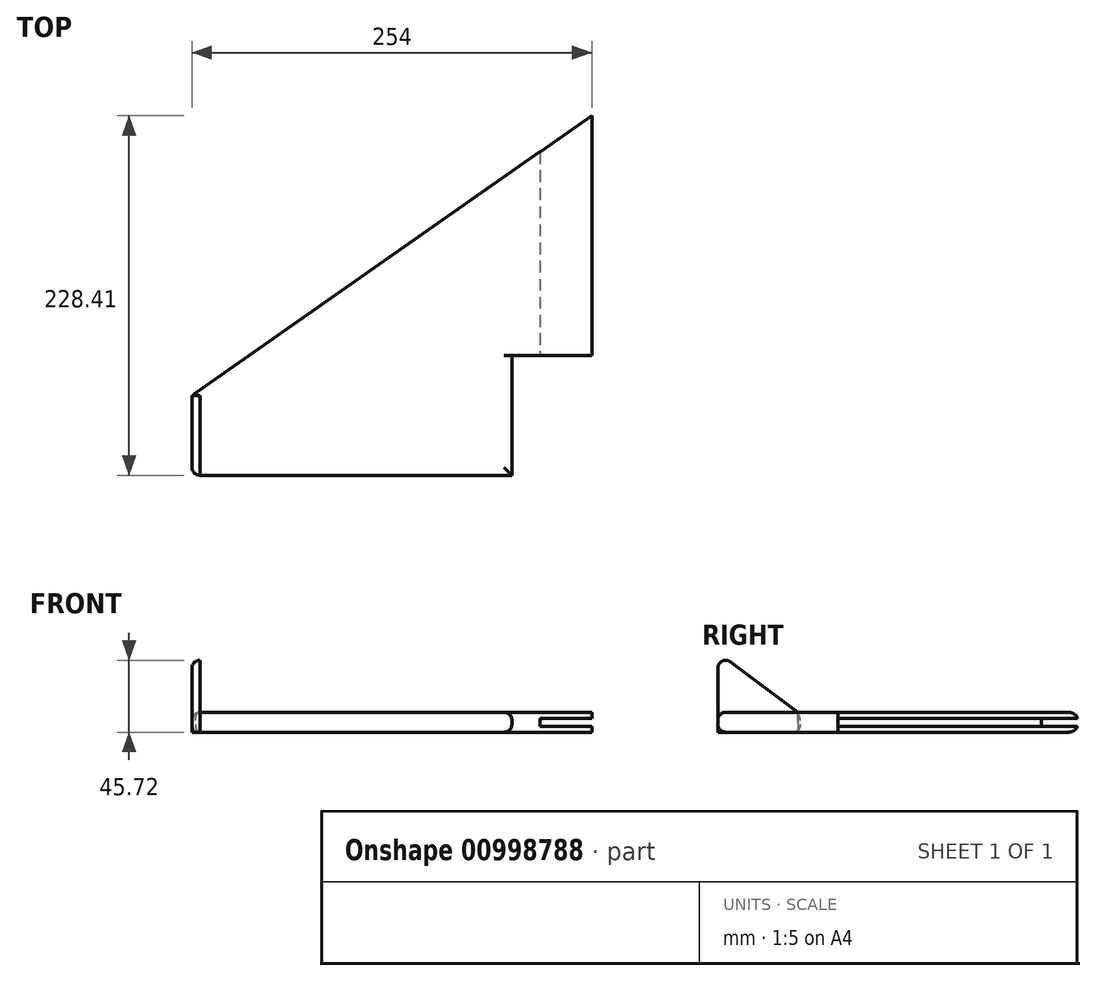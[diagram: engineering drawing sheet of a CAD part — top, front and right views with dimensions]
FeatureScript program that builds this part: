
annotation { "Feature Type Name" : "Feature", "Feature Type Description" : "" }
export const myFeature = defineFeature(function(context is Context, id is Id, definition is map)
    precondition{}
    {
        {
            var Q0;
            Q0=qCreatedBy(makeId("Top.planeOp"),FACE);
            var sketch = newSketch(context, id + "F0", { "sketchPlane" : qUnion([Q0])});
            skLineSegment(sketch, "E0", {"start": v(85.13, 123.88) * mm, "end": v(85.13, -28.52) * mm});
            skLineSegment(sketch, "E1", {"start": v(85.13, -28.52) * mm, "end": v(34.33, -28.52) * mm});
            skLineSegment(sketch, "E2", {"start": v(34.33, -28.52) * mm, "end": v(34.33, -104.72) * mm});
            skLineSegment(sketch, "E3", {"start": v(34.33, -104.72) * mm, "end": v(-168.87, -104.72) * mm});
            skLineSegment(sketch, "E4", {"start": v(-168.87, -104.72) * mm, "end": v(-168.87, -53.92) * mm});
            skLineSegment(sketch, "E5", {"start": v(-168.87, -53.92) * mm, "end": v(85.13, 123.88) * mm});
            skSolve(sketch);
        }
        {
            var Q0;
            Q0=makeQuery(id+"F0.imprint","IMPRINT",FACE,{"disambiguationData":[TD([[makeQuery(id+"F0.imprint","IMPRINT",EDGE,{"derivedFrom":sQuery(id+"F0.wireOp",EDGE,"E0")}),-1.0]])]});
            extrude(context, id + "F1", {"entities" : qUnion([Q0]), "depth" : 12.7 * mm, "offsetDistance" : 25.4 * mm});
        }
        {
            var Q0;
            Q0=makeQuery(id+"F1.opExtrude","SWEPT_FACE",FACE,{"disambiguationData":[OSD([sQuery(id+"F0.wireOp",EDGE,"E4")])]});
            var sketch = newSketch(context, id + "F2", { "sketchPlane" : qUnion([Q0])});
            skLineSegment(sketch, "E6", {"start": v(53.92, 0) * mm, "end": v(53.92, 12.7) * mm});
            skLineSegment(sketch, "E7", {"start": v(53.92, 12.7) * mm, "end": v(104.72, 12.7) * mm});
            skLineSegment(sketch, "E8", {"start": v(104.72, 12.7) * mm, "end": v(104.72, 0) * mm});
            skLineSegment(sketch, "E9", {"start": v(104.72, 0) * mm, "end": v(53.92, 0) * mm});
            skLineSegment(sketch, "E10", {"start": v(104.72, 0) * mm, "end": v(104.72, 50.8) * mm});
            skLineSegment(sketch, "E11", {"start": v(104.72, 50.8) * mm, "end": v(53.92, 12.7) * mm});
            skSolve(sketch);
        }
        {
            var Q0;
            Q0=makeQuery(id+"F2.imprint","IMPRINT",FACE,{"disambiguationData":[TD([[makeQuery(id+"F2.imprint","IMPRINT",EDGE,{"derivedFrom":sQuery(id+"F2.wireOp",EDGE,"E7")}),-1.0]])]});
            var Q1;
            Q1=makeQuery(id+"F2.imprint","IMPRINT",FACE,{"disambiguationData":[TD([[makeQuery(id+"F2.imprint","IMPRINT",EDGE,{"derivedFrom":sQuery(id+"F2.wireOp",EDGE,"E6")}),1.0]])]});
            extrude(context, id + "F3", {"entities" : qUnion([Q0, Q1]), "oppositeDirection" : true, "depth" : 5.08 * mm, "offsetDistance" : 25.4 * mm});
        }
        {
            var Q0;
            Q0=makeQuery(id+"F1.opExtrude","CAP_EDGE",EDGE,{"disambiguationData":[OSD([sQuery(id+"F0.wireOp",EDGE,"E5")])],"isStart":false});
            var Q1;
            Q1=makeQuery(id+"F1.opExtrude","CAP_EDGE",EDGE,{"disambiguationData":[OSD([sQuery(id+"F0.wireOp",EDGE,"E5")])],"isStart":true});
            var Q2;
            Q2=makeQuery(id+"F1.opExtrude","CAP_EDGE",EDGE,{"disambiguationData":[OSD([sQuery(id+"F0.wireOp",EDGE,"E2")])],"isStart":false});
            var Q3;
            Q3=makeQuery(id+"F1.opExtrude","CAP_EDGE",EDGE,{"disambiguationData":[OSD([sQuery(id+"F0.wireOp",EDGE,"E2")])],"isStart":true});
            var Q4;
            Q4=makeQuery(id+"F1.opExtrude","CAP_EDGE",EDGE,{"disambiguationData":[OSD([sQuery(id+"F0.wireOp",EDGE,"E3")])],"isStart":false});
            var Q5;
            Q5=makeQuery(id+"F1.opExtrude","CAP_EDGE",EDGE,{"disambiguationData":[OSD([sQuery(id+"F0.wireOp",EDGE,"E3")])],"isStart":true});
            fillet(context, id + "F4", {"entities" : qUnion([Q0, Q1, Q2, Q3, Q4, Q5]), "radius" : 5.08 * mm, "tangentPropagation" : true, "allowEdgeOverflow" : false});
        }
        {
            var Q0;
            Q0=makeQuery(id+"F1.opExtrude","SWEPT_FACE",FACE,{"disambiguationData":[OSD([sQuery(id+"F0.wireOp",EDGE,"E1")])]});
            var sketch = newSketch(context, id + "F5", { "sketchPlane" : qUnion([Q0])});
            skLineSegment(sketch, "E12.bottom", {"start": v(52.11, 8.9) * mm, "end": v(85.13, 8.9) * mm});
            skLineSegment(sketch, "E12.top", {"start": v(52.11, 3.81) * mm, "end": v(85.13, 3.81) * mm});
            skLineSegment(sketch, "E12.left", {"start": v(52.11, 8.9) * mm, "end": v(52.11, 3.81) * mm});
            skLineSegment(sketch, "E12.right", {"start": v(85.13, 8.9) * mm, "end": v(85.13, 3.81) * mm});
            skSolve(sketch);
        }
        {
            var Q0;
            Q0=makeQuery(id+"F5.imprint","IMPRINT",FACE,{"disambiguationData":[TD([[makeQuery(id+"F5.imprint","IMPRINT",EDGE,{"derivedFrom":sQuery(id+"F5.wireOp",EDGE,"E12.bottom")}),-1.0]])]});
            extrude(context, id + "F6", {"entities" : qUnion([Q0]), "operationType" : NewBodyOperationType.REMOVE, "endBound" : BoundingType.THROUGH_ALL, "oppositeDirection" : true, "depth" : 25.4 * mm, "offsetDistance" : 25.4 * mm});
        }
        {
            var Q0;
            Q0=makeQuery(id+"F3.opExtrude","CAP_EDGE",EDGE,{"disambiguationData":[OSD([sQuery(id+"F2.wireOp",EDGE,"E8"),sQuery(id+"F2.wireOp",EDGE,"E10")])],"isStart":true});
            var Q1;
            Q1=makeQuery(id+"F3.opExtrude","CAP_EDGE",EDGE,{"disambiguationData":[OSD([sQuery(id+"F2.wireOp",EDGE,"E11")])],"isStart":true});
            var Q2;
            Q2=makeQuery(id+"F3.opExtrude","SWEPT_EDGE",EDGE,{"disambiguationData":[OSD([sQuery(id+"F2.wireOp",EDGE,"E10"),sQuery(id+"F2.wireOp",EDGE,"E11")])]});
            var Q3;
            Q3=makeQuery(id+"F1.opExtrude","CAP_EDGE",EDGE,{"disambiguationData":[OSD([sQuery(id+"F0.wireOp",EDGE,"E4")])],"isStart":true});
            fillet(context, id + "F7", {"entities" : qUnion([Q0, Q1, Q2, Q3]), "radius" : 5.08 * mm, "tangentPropagation" : true, "allowEdgeOverflow" : false});
        }
    });
